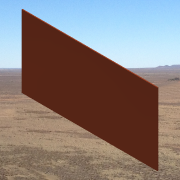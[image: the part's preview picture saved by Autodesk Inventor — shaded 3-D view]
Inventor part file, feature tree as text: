
AUTODESK INVENTOR PART (.ipt)
format: ipt  version: 2014 SP1 (Build 180222100, 222)  size: 109,056 bytes
history: native  units: in
note: dims shown in document units (in); Inventor stores cm internally (conversion verified against a paired STEP export)
features: extrude x1, sketch x1
ambient origin geometry x8: Origin, YZ Plane, XZ Plane, XY Plane, X Axis, Y Axis, Z Axis, Center Point
bodies: Solid1 (feature_tree)
feature tree (2):
  extrude  "Extrusion1"  Depth=8.0in
  sketch  "Sketch1"  dims[d0=15.0in d1=8.0in d2=0.1in d3=0.0in]
